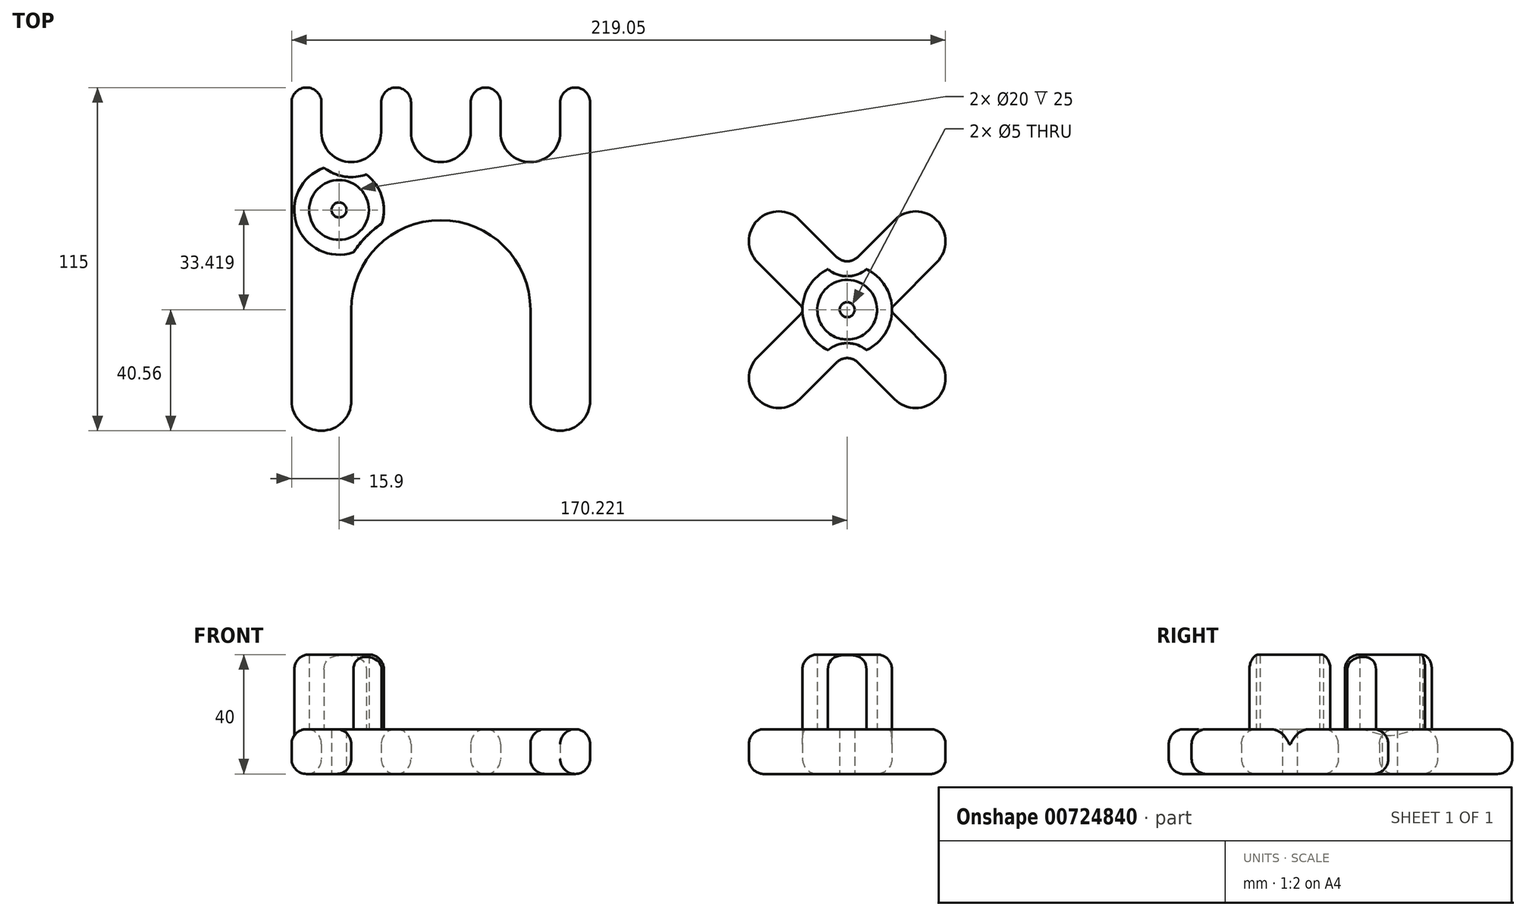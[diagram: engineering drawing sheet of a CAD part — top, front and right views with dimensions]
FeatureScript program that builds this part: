
annotation { "Feature Type Name" : "Feature", "Feature Type Description" : "" }
export const myFeature = defineFeature(function(context is Context, id is Id, definition is map)
    precondition{}
    {
        {
            var Q0;
            Q0=qCreatedBy(makeId("Top.planeOp"),FACE);
            var sketch = newSketch(context, id + "F0", { "sketchPlane" : qUnion([Q0])});
            skArc(sketch, "E0", {"start": v(30, 0) * mm, "mid": v(0, 30) * mm, "end": v(-30, 0) * mm});
            skLineSegment(sketch, "E1", {"start": v(-38.28, -30.56) * mm, "end": v(45.78, -30.56) * mm, "construction": true});
            skLineSegment(sketch, "E2", {"start": v(-30, 0) * mm, "end": v(-30, -30.56) * mm});
            skLineSegment(sketch, "E3", {"start": v(30, 0) * mm, "end": v(30, -30.56) * mm});
            skLineSegment(sketch, "E4", {"start": v(-50, 69.44) * mm, "end": v(-50, -30.56) * mm});
            skLineSegment(sketch, "E5", {"start": v(50, 69.44) * mm, "end": v(50, -30.56) * mm});
            skArc(sketch, "E6", {"start": v(-50, -30.56) * mm, "mid": v(-40, -40.56) * mm, "end": v(-30, -30.56) * mm});
            skArc(sketch, "E7", {"start": v(30, -30.56) * mm, "mid": v(40, -40.56) * mm, "end": v(50, -30.56) * mm});
            skArc(sketch, "E8", {"start": v(-10, 59.44) * mm, "mid": v(0, 49.44) * mm, "end": v(10, 59.44) * mm});
            skArc(sketch, "E9", {"start": v(-10, 69.44) * mm, "mid": v(-15, 74.44) * mm, "end": v(-20, 69.44) * mm});
            skArc(sketch, "E10", {"start": v(20, 69.44) * mm, "mid": v(15, 74.44) * mm, "end": v(10, 69.44) * mm});
            skArc(sketch, "E11", {"start": v(-40, 59.44) * mm, "mid": v(-30, 49.44) * mm, "end": v(-20, 59.44) * mm});
            skArc(sketch, "E12", {"start": v(-40, 69.44) * mm, "mid": v(-45, 74.44) * mm, "end": v(-50, 69.44) * mm});
            skArc(sketch, "E13", {"start": v(20, 59.44) * mm, "mid": v(30, 49.44) * mm, "end": v(40, 59.44) * mm});
            skArc(sketch, "E14", {"start": v(50, 69.44) * mm, "mid": v(45, 74.44) * mm, "end": v(40, 69.44) * mm});
            skLineSegment(sketch, "E15", {"start": v(-40, 69.44) * mm, "end": v(-40, 59.44) * mm});
            skLineSegment(sketch, "E16", {"start": v(-20, 69.44) * mm, "end": v(-20, 59.44) * mm});
            skLineSegment(sketch, "E17", {"start": v(-10, 69.44) * mm, "end": v(-10, 59.44) * mm});
            skLineSegment(sketch, "E18", {"start": v(10, 69.44) * mm, "end": v(10, 59.44) * mm});
            skLineSegment(sketch, "E19", {"start": v(20, 69.44) * mm, "end": v(20, 59.44) * mm});
            skLineSegment(sketch, "E20", {"start": v(40, 69.44) * mm, "end": v(40, 59.44) * mm});
            skSolve(sketch);
        }
        {
            var Q0;
            Q0=makeQuery(id+"F0.imprint","IMPRINT",FACE,{"disambiguationData":[TD([[makeQuery(id+"F0.imprint","IMPRINT",EDGE,{"derivedFrom":sQuery(id+"F0.wireOp",EDGE,"E0")}),-1.0]])]});
            extrude(context, id + "F1", {"entities" : qUnion([Q0]), "depth" : 15 * mm, "offsetDistance" : 25 * mm});
        }
        {
            var Q0;
            Q0=makeQuery(id+"F1.opExtrude","CAP_FACE",FACE,{"disambiguationData":[OSD([sQuery(id+"F0.wireOp",EDGE,"E0"),sQuery(id+"F0.wireOp",EDGE,"E2"),sQuery(id+"F0.wireOp",EDGE,"E3"),sQuery(id+"F0.wireOp",EDGE,"E4"),sQuery(id+"F0.wireOp",EDGE,"E5"),sQuery(id+"F0.wireOp",EDGE,"E6"),sQuery(id+"F0.wireOp",EDGE,"E7"),sQuery(id+"F0.wireOp",EDGE,"E8"),sQuery(id+"F0.wireOp",EDGE,"E11"),sQuery(id+"F0.wireOp",EDGE,"E12"),sQuery(id+"F0.wireOp",EDGE,"E9"),sQuery(id+"F0.wireOp",EDGE,"E13"),sQuery(id+"F0.wireOp",EDGE,"E10"),sQuery(id+"F0.wireOp",EDGE,"E14"),sQuery(id+"F0.wireOp",EDGE,"E15"),sQuery(id+"F0.wireOp",EDGE,"E16"),sQuery(id+"F0.wireOp",EDGE,"E17"),sQuery(id+"F0.wireOp",EDGE,"E18"),sQuery(id+"F0.wireOp",EDGE,"E19"),sQuery(id+"F0.wireOp",EDGE,"E20")])],"isStart":false});
            fillet(context, id + "F2", {"entities" : qUnion([Q0]), "radius" : 5 * mm, "tangentPropagation" : true, "allowEdgeOverflow" : false});
        }
        {
            var Q0;
            Q0=makeQuery(id+"F1.opExtrude","CAP_FACE",FACE,{"disambiguationData":[OSD([sQuery(id+"F0.wireOp",EDGE,"E0"),sQuery(id+"F0.wireOp",EDGE,"E2"),sQuery(id+"F0.wireOp",EDGE,"E3"),sQuery(id+"F0.wireOp",EDGE,"E4"),sQuery(id+"F0.wireOp",EDGE,"E5"),sQuery(id+"F0.wireOp",EDGE,"E6"),sQuery(id+"F0.wireOp",EDGE,"E7"),sQuery(id+"F0.wireOp",EDGE,"E8"),sQuery(id+"F0.wireOp",EDGE,"E11"),sQuery(id+"F0.wireOp",EDGE,"E12"),sQuery(id+"F0.wireOp",EDGE,"E9"),sQuery(id+"F0.wireOp",EDGE,"E13"),sQuery(id+"F0.wireOp",EDGE,"E10"),sQuery(id+"F0.wireOp",EDGE,"E14"),sQuery(id+"F0.wireOp",EDGE,"E15"),sQuery(id+"F0.wireOp",EDGE,"E16"),sQuery(id+"F0.wireOp",EDGE,"E17"),sQuery(id+"F0.wireOp",EDGE,"E18"),sQuery(id+"F0.wireOp",EDGE,"E19"),sQuery(id+"F0.wireOp",EDGE,"E20")])],"isStart":true});
            fillet(context, id + "F3", {"entities" : qUnion([Q0]), "radius" : 5 * mm, "tangentPropagation" : true, "allowEdgeOverflow" : false});
        }
        {
            var Q0;
            Q0=makeQuery(id+"F1.opExtrude","CAP_FACE",FACE,{"disambiguationData":[OSD([sQuery(id+"F0.wireOp",EDGE,"E0"),sQuery(id+"F0.wireOp",EDGE,"E2"),sQuery(id+"F0.wireOp",EDGE,"E3"),sQuery(id+"F0.wireOp",EDGE,"E4"),sQuery(id+"F0.wireOp",EDGE,"E5"),sQuery(id+"F0.wireOp",EDGE,"E6"),sQuery(id+"F0.wireOp",EDGE,"E7"),sQuery(id+"F0.wireOp",EDGE,"E8"),sQuery(id+"F0.wireOp",EDGE,"E11"),sQuery(id+"F0.wireOp",EDGE,"E12"),sQuery(id+"F0.wireOp",EDGE,"E9"),sQuery(id+"F0.wireOp",EDGE,"E13"),sQuery(id+"F0.wireOp",EDGE,"E10"),sQuery(id+"F0.wireOp",EDGE,"E14"),sQuery(id+"F0.wireOp",EDGE,"E15"),sQuery(id+"F0.wireOp",EDGE,"E16"),sQuery(id+"F0.wireOp",EDGE,"E17"),sQuery(id+"F0.wireOp",EDGE,"E18"),sQuery(id+"F0.wireOp",EDGE,"E19"),sQuery(id+"F0.wireOp",EDGE,"E20")])],"isStart":false});
            var sketch = newSketch(context, id + "F4", { "sketchPlane" : qUnion([Q0])});
            skCircle(sketch, "E21", {"center": v(-34.1, 33.42) * mm, "radius": 10 * mm});
            skCircle(sketch, "E22", {"center": v(-34.1, 33.42) * mm, "radius": 15 * mm});
            skSolve(sketch);
        }
        {
            var Q0;
            Q0=makeQuery(id+"F4.imprint","IMPRINT",FACE,{"disambiguationData":[TD([[makeQuery(id+"F4.imprint","IMPRINT",EDGE,{"derivedFrom":sQuery(id+"F4.wireOp",EDGE,"E21")}),-1.0]])]});
            var Q1;
            {var subQ0=sQuery(id+"F4.wireOp",EDGE,"E22");var subQ1=sQuery(id+"F0.wireOp",EDGE,"E4");var subQ2=makeQuery(id+"F2.opFillet","BLEND_EDGE",EDGE,{"blendedFrom":[makeQuery(id+"F1.opExtrude","CAP_EDGE",EDGE,{"disambiguationData":[OSD([subQ1])],"isStart":false}),makeQuery(id+"F1.opExtrude","CAP_FACE",FACE,{"disambiguationData":[OSD([sQuery(id+"F0.wireOp",EDGE,"E0"),sQuery(id+"F0.wireOp",EDGE,"E2"),sQuery(id+"F0.wireOp",EDGE,"E3"),subQ1,sQuery(id+"F0.wireOp",EDGE,"E5"),sQuery(id+"F0.wireOp",EDGE,"E6"),sQuery(id+"F0.wireOp",EDGE,"E7"),sQuery(id+"F0.wireOp",EDGE,"E8"),sQuery(id+"F0.wireOp",EDGE,"E11"),sQuery(id+"F0.wireOp",EDGE,"E12"),sQuery(id+"F0.wireOp",EDGE,"E9"),sQuery(id+"F0.wireOp",EDGE,"E13"),sQuery(id+"F0.wireOp",EDGE,"E10"),sQuery(id+"F0.wireOp",EDGE,"E14"),sQuery(id+"F0.wireOp",EDGE,"E15"),sQuery(id+"F0.wireOp",EDGE,"E16"),sQuery(id+"F0.wireOp",EDGE,"E17"),sQuery(id+"F0.wireOp",EDGE,"E18"),sQuery(id+"F0.wireOp",EDGE,"E19"),sQuery(id+"F0.wireOp",EDGE,"E20")])],"isStart":false})],"blendedInto":[makeQuery(id+"F1.opExtrude","CAP_FACE",FACE,{"disambiguationData":[OSD([sQuery(id+"F0.wireOp",EDGE,"E0"),sQuery(id+"F0.wireOp",EDGE,"E2"),sQuery(id+"F0.wireOp",EDGE,"E3"),subQ1,sQuery(id+"F0.wireOp",EDGE,"E5"),sQuery(id+"F0.wireOp",EDGE,"E6"),sQuery(id+"F0.wireOp",EDGE,"E7"),sQuery(id+"F0.wireOp",EDGE,"E8"),sQuery(id+"F0.wireOp",EDGE,"E11"),sQuery(id+"F0.wireOp",EDGE,"E12"),sQuery(id+"F0.wireOp",EDGE,"E9"),sQuery(id+"F0.wireOp",EDGE,"E13"),sQuery(id+"F0.wireOp",EDGE,"E10"),sQuery(id+"F0.wireOp",EDGE,"E14"),sQuery(id+"F0.wireOp",EDGE,"E15"),sQuery(id+"F0.wireOp",EDGE,"E16"),sQuery(id+"F0.wireOp",EDGE,"E17"),sQuery(id+"F0.wireOp",EDGE,"E18"),sQuery(id+"F0.wireOp",EDGE,"E19"),sQuery(id+"F0.wireOp",EDGE,"E20")])],"isStart":false})]});var subQ3=makeQuery(id+"F4.imprint","INTERSECT",VERTEX,{"disambiguationData":[OD(0.0)],"derivedFrom":[subQ2,subQ0]});Q1=makeQuery(id+"F4.imprint","IMPRINT",FACE,{"disambiguationData":[TD([[makeQuery(id+"F4.imprint","IMPRINT",EDGE,{"disambiguationData":[TD([[subQ3,-1.0]])],"derivedFrom":subQ0}),1.0]])]});}
            extrude(context, id + "F5", {"entities" : qUnion([Q0, Q1]), "operationType" : NewBodyOperationType.ADD, "depth" : 25 * mm, "offsetDistance" : 25 * mm, "hasSecondDirection" : true, "secondDirectionOppositeDirection" : true, "secondDirectionDepth" : 10 * mm});
        }
        {
            var Q0;
            Q0=makeQuery(id+"F5.opExtrude","CAP_EDGE",EDGE,{"disambiguationData":[OSD([sQuery(id+"F4.wireOp",EDGE,"E22")])],"isStart":false});
            fillet(context, id + "F6", {"entities" : qUnion([Q0]), "radius" : 5 * mm, "tangentPropagation" : true, "allowEdgeOverflow" : false});
        }
        {
            var Q0;
            Q0=qCreatedBy(makeId("Top.planeOp"),FACE);
            var sketch = newSketch(context, id + "F7", { "sketchPlane" : qUnion([Q0])});
            skCircle(sketch, "E23", {"center": v(136.12, 0) * mm, "radius": 30 * mm, "construction": true});
            skLineSegment(sketch, "E24", {"start": v(75.4, -30) * mm, "end": v(194.97, -30) * mm, "construction": true});
            skLineSegment(sketch, "E25", {"start": v(76.2, 30) * mm, "end": v(194.43, 30) * mm, "construction": true});
            skLineSegment(sketch, "E26", {"start": v(106.12, 30) * mm, "end": v(166.12, -30) * mm, "construction": true});
            skLineSegment(sketch, "E27", {"start": v(106.12, -30) * mm, "end": v(166.12, 30) * mm, "construction": true});
            skLineSegment(sketch, "E28.left", {"start": v(106.12, -15.86) * mm, "end": v(120.56, -1.41) * mm});
            skLineSegment(sketch, "E28.right", {"start": v(120.26, -30) * mm, "end": v(132.59, -17.68) * mm});
            skLineSegment(sketch, "E29.left", {"start": v(106.12, 15.86) * mm, "end": v(120.56, 1.41) * mm});
            skLineSegment(sketch, "E29.right", {"start": v(120.26, 30) * mm, "end": v(132.59, 17.68) * mm});
            skLineSegment(sketch, "E30.trimOffspring", {"start": v(139.66, 17.68) * mm, "end": v(151.98, 30) * mm});
            skLineSegment(sketch, "E31.trimOffspring", {"start": v(139.66, -17.68) * mm, "end": v(151.98, -30) * mm});
            skLineSegment(sketch, "E32.trimOffspring", {"start": v(151.68, -1.41) * mm, "end": v(166.12, -15.86) * mm});
            skLineSegment(sketch, "E33.trimOffspring", {"start": v(151.68, 1.41) * mm, "end": v(166.12, 15.86) * mm});
            skPoint(sketch, "E34.visualSharp", {"position": v(136.12, 14.14) * mm});
            skArc(sketch, "E34.filletArc", {"start": v(132.59, 17.68) * mm, "mid": v(136.12, 16.21) * mm, "end": v(139.66, 17.68) * mm});
            skPoint(sketch, "E35.visualSharp", {"position": v(121.98, 0) * mm});
            skArc(sketch, "E35.filletArc", {"start": v(120.56, -1.41) * mm, "mid": v(121.15, 0) * mm, "end": v(120.56, 1.41) * mm});
            skPoint(sketch, "E36.visualSharp", {"position": v(150.26, 0) * mm});
            skArc(sketch, "E36.filletArc", {"start": v(151.68, 1.41) * mm, "mid": v(151.1, 0) * mm, "end": v(151.68, -1.41) * mm});
            skPoint(sketch, "E37.visualSharp", {"position": v(136.12, -14.14) * mm});
            skArc(sketch, "E37.filletArc", {"start": v(139.66, -17.68) * mm, "mid": v(136.12, -16.21) * mm, "end": v(132.59, -17.68) * mm});
            skArc(sketch, "E38", {"start": v(166.12, 15.86) * mm, "mid": v(166.12, 30) * mm, "end": v(151.98, 30) * mm});
            skArc(sketch, "E39", {"start": v(120.26, 30) * mm, "mid": v(106.12, 30) * mm, "end": v(106.12, 15.86) * mm});
            skArc(sketch, "E40", {"start": v(151.98, -30) * mm, "mid": v(166.12, -30) * mm, "end": v(166.12, -15.86) * mm});
            skArc(sketch, "E41", {"start": v(106.12, -15.86) * mm, "mid": v(106.12, -30) * mm, "end": v(120.26, -30) * mm});
            skSolve(sketch);
        }
        {
            var Q0;
            Q0 = qSketchRegion(id + "F7", true);
            extrude(context, id + "F8", {"entities" : qUnion([Q0]), "depth" : 15 * mm, "offsetDistance" : 25 * mm});
        }
        {
            var Q0;
            Q0=makeQuery(id+"F8.opExtrude","CAP_FACE",FACE,{"disambiguationData":[OSD([sQuery(id+"F7.wireOp",EDGE,"E28.left"),sQuery(id+"F7.wireOp",EDGE,"E28.right"),sQuery(id+"F7.wireOp",EDGE,"E29.left"),sQuery(id+"F7.wireOp",EDGE,"E29.right"),sQuery(id+"F7.wireOp",EDGE,"E30.trimOffspring"),sQuery(id+"F7.wireOp",EDGE,"E31.trimOffspring"),sQuery(id+"F7.wireOp",EDGE,"E32.trimOffspring"),sQuery(id+"F7.wireOp",EDGE,"E33.trimOffspring"),sQuery(id+"F7.wireOp",EDGE,"E34.filletArc"),sQuery(id+"F7.wireOp",EDGE,"E35.filletArc"),sQuery(id+"F7.wireOp",EDGE,"E36.filletArc"),sQuery(id+"F7.wireOp",EDGE,"E37.filletArc"),sQuery(id+"F7.wireOp",EDGE,"E38"),sQuery(id+"F7.wireOp",EDGE,"E39"),sQuery(id+"F7.wireOp",EDGE,"E40"),sQuery(id+"F7.wireOp",EDGE,"E41")])],"isStart":false});
            fillet(context, id + "F9", {"entities" : qUnion([Q0]), "radius" : 5 * mm, "tangentPropagation" : true, "allowEdgeOverflow" : false});
        }
        {
            var Q0;
            Q0=makeQuery(id+"F8.opExtrude","CAP_FACE",FACE,{"disambiguationData":[OSD([sQuery(id+"F7.wireOp",EDGE,"E28.left"),sQuery(id+"F7.wireOp",EDGE,"E28.right"),sQuery(id+"F7.wireOp",EDGE,"E29.left"),sQuery(id+"F7.wireOp",EDGE,"E29.right"),sQuery(id+"F7.wireOp",EDGE,"E30.trimOffspring"),sQuery(id+"F7.wireOp",EDGE,"E31.trimOffspring"),sQuery(id+"F7.wireOp",EDGE,"E32.trimOffspring"),sQuery(id+"F7.wireOp",EDGE,"E33.trimOffspring"),sQuery(id+"F7.wireOp",EDGE,"E34.filletArc"),sQuery(id+"F7.wireOp",EDGE,"E35.filletArc"),sQuery(id+"F7.wireOp",EDGE,"E36.filletArc"),sQuery(id+"F7.wireOp",EDGE,"E37.filletArc"),sQuery(id+"F7.wireOp",EDGE,"E38"),sQuery(id+"F7.wireOp",EDGE,"E39"),sQuery(id+"F7.wireOp",EDGE,"E40"),sQuery(id+"F7.wireOp",EDGE,"E41")])],"isStart":true});
            fillet(context, id + "F10", {"entities" : qUnion([Q0]), "radius" : 5 * mm, "tangentPropagation" : true, "allowEdgeOverflow" : false});
        }
        {
            var Q0;
            Q0=makeQuery(id+"F8.opExtrude","CAP_FACE",FACE,{"disambiguationData":[OSD([sQuery(id+"F7.wireOp",EDGE,"E28.left"),sQuery(id+"F7.wireOp",EDGE,"E28.right"),sQuery(id+"F7.wireOp",EDGE,"E29.left"),sQuery(id+"F7.wireOp",EDGE,"E29.right"),sQuery(id+"F7.wireOp",EDGE,"E30.trimOffspring"),sQuery(id+"F7.wireOp",EDGE,"E31.trimOffspring"),sQuery(id+"F7.wireOp",EDGE,"E32.trimOffspring"),sQuery(id+"F7.wireOp",EDGE,"E33.trimOffspring"),sQuery(id+"F7.wireOp",EDGE,"E34.filletArc"),sQuery(id+"F7.wireOp",EDGE,"E35.filletArc"),sQuery(id+"F7.wireOp",EDGE,"E36.filletArc"),sQuery(id+"F7.wireOp",EDGE,"E37.filletArc"),sQuery(id+"F7.wireOp",EDGE,"E38"),sQuery(id+"F7.wireOp",EDGE,"E39"),sQuery(id+"F7.wireOp",EDGE,"E40"),sQuery(id+"F7.wireOp",EDGE,"E41")])],"isStart":false});
            var sketch = newSketch(context, id + "F11", { "sketchPlane" : qUnion([Q0])});
            skCircle(sketch, "E42", {"center": v(136.12, 0) * mm, "radius": 10 * mm});
            skCircle(sketch, "E43", {"center": v(136.12, 0) * mm, "radius": 15 * mm});
            skSolve(sketch);
        }
        {
            var Q0;
            Q0=makeQuery(id+"F11.imprint","IMPRINT",FACE,{"disambiguationData":[TD([[makeQuery(id+"F11.imprint","IMPRINT",EDGE,{"derivedFrom":sQuery(id+"F11.wireOp",EDGE,"E42")}),-1.0]])]});
            var Q1;
            {var subQ0=sQuery(id+"F7.wireOp",EDGE,"E36.filletArc");var subQ1=sQuery(id+"F7.wireOp",EDGE,"E35.filletArc");var subQ2=sQuery(id+"F7.wireOp",EDGE,"E34.filletArc");var subQ3=sQuery(id+"F7.wireOp",EDGE,"E33.trimOffspring");var subQ4=sQuery(id+"F7.wireOp",EDGE,"E29.left");var subQ5=makeQuery(id+"F8.opExtrude","CAP_FACE",FACE,{"disambiguationData":[OSD([sQuery(id+"F7.wireOp",EDGE,"E28.left"),sQuery(id+"F7.wireOp",EDGE,"E28.right"),subQ4,sQuery(id+"F7.wireOp",EDGE,"E29.right"),sQuery(id+"F7.wireOp",EDGE,"E30.trimOffspring"),sQuery(id+"F7.wireOp",EDGE,"E31.trimOffspring"),sQuery(id+"F7.wireOp",EDGE,"E32.trimOffspring"),subQ3,subQ2,subQ1,subQ0,sQuery(id+"F7.wireOp",EDGE,"E37.filletArc"),sQuery(id+"F7.wireOp",EDGE,"E38"),sQuery(id+"F7.wireOp",EDGE,"E39"),sQuery(id+"F7.wireOp",EDGE,"E40"),sQuery(id+"F7.wireOp",EDGE,"E41")])],"isStart":false});var subQ6=makeQuery(id+"F9.opFillet","BLEND_EDGE",EDGE,{"blendedFrom":[makeQuery(id+"F8.opExtrude","CAP_EDGE",EDGE,{"disambiguationData":[OSD([subQ1])],"isStart":false}),subQ5],"blendedInto":[subQ5]});var subQ16=sQuery(id+"F11.wireOp",EDGE,"E42");var subQ17=makeQuery(id+"F11.imprint","INTERSECT",VERTEX,{"disambiguationData":[OD(0.0)],"derivedFrom":[subQ6,subQ16]});Q1=makeQuery(id+"F11.imprint","IMPRINT",FACE,{"disambiguationData":[TD([[makeQuery(id+"F11.imprint","IMPRINT",EDGE,{"disambiguationData":[TD([[subQ17,1.0]])],"derivedFrom":subQ16}),-1.0]])]});}
            var Q2;
            {var subQ0=sQuery(id+"F7.wireOp",EDGE,"E37.filletArc");var subQ1=sQuery(id+"F7.wireOp",EDGE,"E36.filletArc");var subQ2=sQuery(id+"F7.wireOp",EDGE,"E35.filletArc");var subQ3=sQuery(id+"F7.wireOp",EDGE,"E32.trimOffspring");var subQ4=sQuery(id+"F7.wireOp",EDGE,"E28.left");var subQ5=makeQuery(id+"F8.opExtrude","CAP_FACE",FACE,{"disambiguationData":[OSD([subQ4,sQuery(id+"F7.wireOp",EDGE,"E28.right"),sQuery(id+"F7.wireOp",EDGE,"E29.left"),sQuery(id+"F7.wireOp",EDGE,"E29.right"),sQuery(id+"F7.wireOp",EDGE,"E30.trimOffspring"),sQuery(id+"F7.wireOp",EDGE,"E31.trimOffspring"),subQ3,sQuery(id+"F7.wireOp",EDGE,"E33.trimOffspring"),sQuery(id+"F7.wireOp",EDGE,"E34.filletArc"),subQ2,subQ1,subQ0,sQuery(id+"F7.wireOp",EDGE,"E38"),sQuery(id+"F7.wireOp",EDGE,"E39"),sQuery(id+"F7.wireOp",EDGE,"E40"),sQuery(id+"F7.wireOp",EDGE,"E41")])],"isStart":false});var subQ6=makeQuery(id+"F9.opFillet","BLEND_EDGE",EDGE,{"blendedFrom":[makeQuery(id+"F8.opExtrude","CAP_EDGE",EDGE,{"disambiguationData":[OSD([subQ2])],"isStart":false}),subQ5],"blendedInto":[subQ5]});var subQ16=sQuery(id+"F11.wireOp",EDGE,"E42");var subQ17=makeQuery(id+"F11.imprint","INTERSECT",VERTEX,{"disambiguationData":[OD(1.0)],"derivedFrom":[subQ6,subQ16]});Q2=makeQuery(id+"F11.imprint","IMPRINT",FACE,{"disambiguationData":[TD([[makeQuery(id+"F11.imprint","IMPRINT",EDGE,{"disambiguationData":[TD([[subQ17,-1.0]])],"derivedFrom":subQ16}),-1.0]])]});}
            extrude(context, id + "F12", {"entities" : qUnion([Q0, Q1, Q2]), "operationType" : NewBodyOperationType.ADD, "depth" : 25 * mm, "offsetDistance" : 25 * mm, "hasSecondDirection" : true, "secondDirectionOppositeDirection" : true, "secondDirectionDepth" : 5 * mm});
        }
        {
            var Q0;
            {var subQ0=sQuery(id+"F11.wireOp",EDGE,"E43");var subQ1=sQuery(id+"F7.wireOp",EDGE,"E37.filletArc");var subQ2=sQuery(id+"F7.wireOp",EDGE,"E36.filletArc");var subQ3=makeQuery(id+"F8.opExtrude","CAP_FACE",FACE,{"disambiguationData":[OSD([sQuery(id+"F7.wireOp",EDGE,"E28.left"),sQuery(id+"F7.wireOp",EDGE,"E28.right"),sQuery(id+"F7.wireOp",EDGE,"E29.left"),sQuery(id+"F7.wireOp",EDGE,"E29.right"),sQuery(id+"F7.wireOp",EDGE,"E30.trimOffspring"),sQuery(id+"F7.wireOp",EDGE,"E31.trimOffspring"),sQuery(id+"F7.wireOp",EDGE,"E32.trimOffspring"),sQuery(id+"F7.wireOp",EDGE,"E33.trimOffspring"),sQuery(id+"F7.wireOp",EDGE,"E34.filletArc"),sQuery(id+"F7.wireOp",EDGE,"E35.filletArc"),subQ2,subQ1,sQuery(id+"F7.wireOp",EDGE,"E38"),sQuery(id+"F7.wireOp",EDGE,"E39"),sQuery(id+"F7.wireOp",EDGE,"E40"),sQuery(id+"F7.wireOp",EDGE,"E41")])],"isStart":false});Q0=makeQuery(id+"F12.opExtrude","CAP_EDGE",EDGE,{"disambiguationData":[OSD([subQ0]),TDD([makeQuery(id+"F11.imprint","IMPRINT",EDGE,{"disambiguationData":[TD([[makeQuery(id+"F11.imprint","INTERSECT",VERTEX,{"disambiguationData":[OD(1.0)],"derivedFrom":[makeQuery(id+"F9.opFillet","BLEND_EDGE",EDGE,{"blendedFrom":[makeQuery(id+"F8.opExtrude","CAP_EDGE",EDGE,{"disambiguationData":[OSD([subQ1])],"isStart":false}),subQ3],"blendedInto":[subQ3]}),subQ0]}),-1.0]])],"derivedFrom":subQ0})])],"isStart":false});}
            fillet(context, id + "F13", {"entities" : qUnion([Q0]), "radius" : 5 * mm, "tangentPropagation" : true, "allowEdgeOverflow" : false});
        }
        {
            var Q0;
            Q0=qCreatedBy(makeId("Top.planeOp"),FACE);
            var sketch = newSketch(context, id + "F14", { "sketchPlane" : qUnion([Q0])});
            skCircle(sketch, "E44", {"center": v(136.12, 0) * mm, "radius": 2.5 * mm});
            skSolve(sketch);
        }
        {
            var Q0;
            Q0 = qSketchRegion(id + "F14", true);
            extrude(context, id + "F15", {"entities" : qUnion([Q0]), "operationType" : NewBodyOperationType.REMOVE, "depth" : 25 * mm, "offsetDistance" : 25 * mm});
        }
        {
            var Q0;
            Q0=qCreatedBy(makeId("Top.planeOp"),FACE);
            var sketch = newSketch(context, id + "F16", { "sketchPlane" : qUnion([Q0])});
            skCircle(sketch, "E45", {"center": v(-34.1, 33.42) * mm, "radius": 2.5 * mm});
            skSolve(sketch);
        }
        {
            var Q0;
            Q0 = qSketchRegion(id + "F16", true);
            extrude(context, id + "F17", {"entities" : qUnion([Q0]), "operationType" : NewBodyOperationType.REMOVE, "depth" : 25 * mm, "offsetDistance" : 25 * mm});
        }
    });
